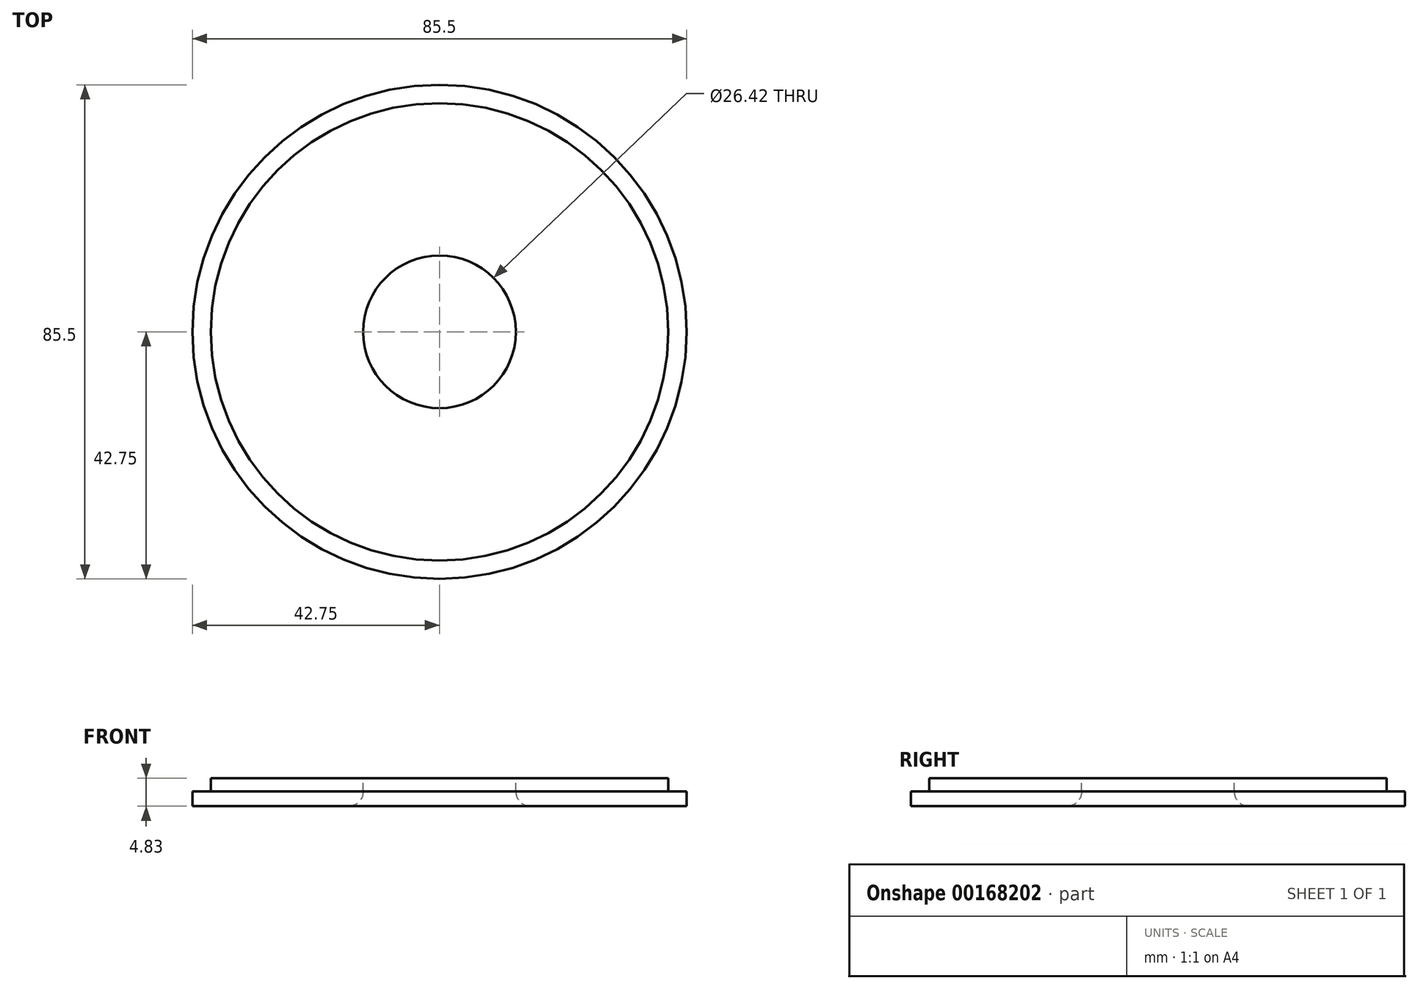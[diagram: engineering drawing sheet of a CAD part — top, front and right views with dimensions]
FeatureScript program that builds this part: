
annotation { "Feature Type Name" : "Feature", "Feature Type Description" : "" }
export const myFeature = defineFeature(function(context is Context, id is Id, definition is map)
    precondition{}
    {
        {
            var Q0;
            Q0=qCreatedBy(makeId("Top.planeOp"),FACE);
            var sketch = newSketch(context, id + "F0", { "sketchPlane" : qUnion([Q0])});
            skCircle(sketch, "E0", {"center": v(0, 0) * mm, "radius": 42.75 * mm});
            skSolve(sketch);
        }
        {
            var Q0;
            Q0=qSketchRegion(id+"F0",true);
            extrude(context, id + "F1", {"entities" : qUnion([Q0]), "depth" : 2.54 * mm});
        }
        {
            var Q0;
            Q0=makeQuery(id+"F1.opExtrude","CAP_FACE",FACE,{"disambiguationData":[OSD([sQuery(id+"F0.wireOp",EDGE,"E0")])],"isStart":false});
            var sketch = newSketch(context, id + "F2", { "sketchPlane" : qUnion([Q0])});
            skCircle(sketch, "E1", {"center": v(0, 0) * mm, "radius": 39.57 * mm});
            skSolve(sketch);
        }
        {
            var Q0;
            Q0=qSketchRegion(id+"F2",true);
            extrude(context, id + "F3", {"entities" : qUnion([Q0]), "operationType" : NewBodyOperationType.ADD, "depth" : 2.3 * mm});
        }
        {
            var Q0;
            Q0=makeQuery(id+"F3.opExtrude","CAP_FACE",FACE,{"disambiguationData":[OSD([sQuery(id+"F2.wireOp",EDGE,"E1")])],"isStart":false});
            var sketch = newSketch(context, id + "F4", { "sketchPlane" : qUnion([Q0])});
            skCircle(sketch, "E2", {"center": v(0, 0) * mm, "radius": 13.2 * mm});
            skSolve(sketch);
        }
        {
            var Q0;
            Q0=qSketchRegion(id+"F4",true);
            extrude(context, id + "F5", {"entities" : qUnion([Q0]), "operationType" : NewBodyOperationType.REMOVE, "endBound" : BoundingType.THROUGH_ALL, "oppositeDirection" : true, "depth" : 25.4 * mm});
        }
        {
            var Q0;
            Q0=makeQuery(id+"F5.boolean.opBoolean","INTERSECT",EDGE,{"derivedFrom":[makeQuery(id+"F1.opExtrude","CAP_FACE",FACE,{"disambiguationData":[OSD([sQuery(id+"F0.wireOp",EDGE,"E0")])],"isStart":true}),makeQuery(id+"F5.opExtrude","SWEPT_FACE",FACE,{"disambiguationData":[OSD([sQuery(id+"F4.wireOp",EDGE,"E2")])]})]});
            fillet(context, id + "F6", {"entities" : qUnion([Q0]), "radius" : 2.54 * mm, "tangentPropagation" : true, "allowEdgeOverflow" : false});
        }
    });
